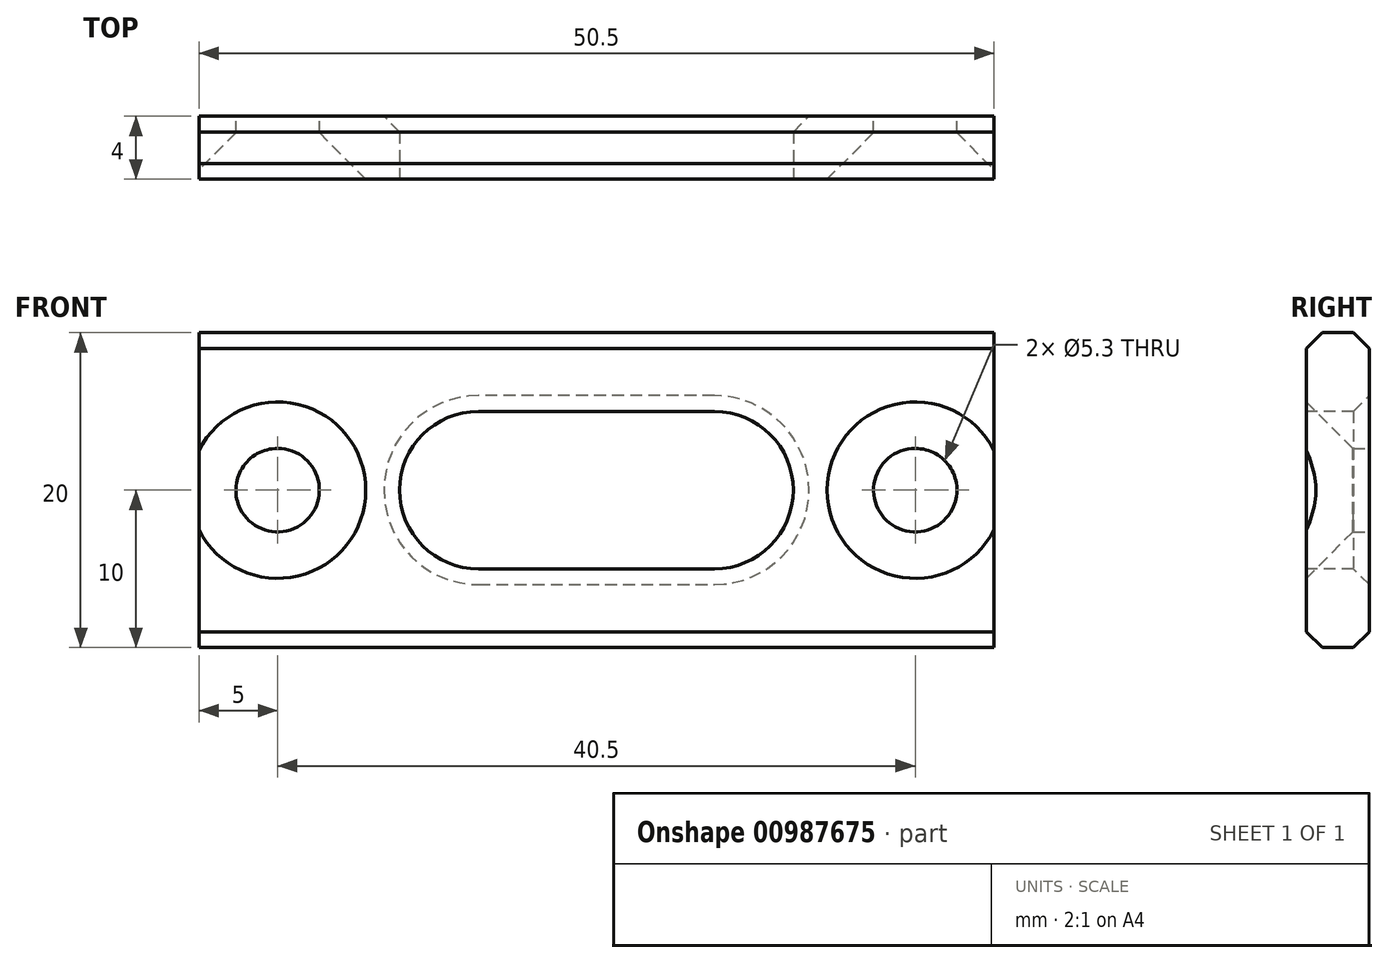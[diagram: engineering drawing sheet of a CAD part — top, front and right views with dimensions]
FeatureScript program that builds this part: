
annotation { "Feature Type Name" : "Feature", "Feature Type Description" : "" }
export const myFeature = defineFeature(function(context is Context, id is Id, definition is map)
    precondition{}
    {
        {
            var Q0;
            Q0=qCreatedBy(makeId("Front.planeOp"),FACE);
            var sketch = newSketch(context, id + "F0", { "sketchPlane" : qUnion([Q0])});
            skLineSegment(sketch, "E0.bottom", {"start": v(-25.25, 0) * mm, "end": v(25.25, 0) * mm});
            skLineSegment(sketch, "E0.top", {"start": v(-25.25, -20) * mm, "end": v(25.25, -20) * mm});
            skLineSegment(sketch, "E0.left", {"start": v(-25.25, 0) * mm, "end": v(-25.25, -20) * mm});
            skLineSegment(sketch, "E0.right", {"start": v(25.25, 0) * mm, "end": v(25.25, -20) * mm});
            skSolve(sketch);
        }
        {
            var Q0;
            Q0=makeQuery(id+"F0.imprint","IMPRINT",FACE,{"disambiguationData":[TD([[makeQuery(id+"F0.imprint","IMPRINT",EDGE,{"derivedFrom":sQuery(id+"F0.wireOp",EDGE,"E0.bottom")}),-1.0]])]});
            extrude(context, id + "F1", {"entities" : qUnion([Q0]), "depth" : 4 * mm, "offsetDistance" : 25 * mm});
        }
        {
            var Q0;
            Q0=makeQuery(id+"F1.opExtrude","CAP_FACE",FACE,{"disambiguationData":[OSD([sQuery(id+"F0.wireOp",EDGE,"E0.bottom"),sQuery(id+"F0.wireOp",EDGE,"E0.top"),sQuery(id+"F0.wireOp",EDGE,"E0.left"),sQuery(id+"F0.wireOp",EDGE,"E0.right")])],"isStart":false});
            var sketch = newSketch(context, id + "F2", { "sketchPlane" : qUnion([Q0])});
            skPoint(sketch, "E1", {"position": v(-20.25, -10) * mm});
            skPoint(sketch, "E2", {"position": v(20.25, -10) * mm});
            skSolve(sketch);
        }
        {
            var Q0;
            Q0=sQuery(id+"F2.wireOp",VERTEX,"E1");
            var Q1;
            Q1=sQuery(id+"F2.wireOp",VERTEX,"E2");
            var Q2;
            Q2=makeQuery(id+"F1.opExtrude","SWEPT_BODY",BODY,{"disambiguationData":[OSD([sQuery(id+"F0.wireOp",EDGE,"E0.bottom"),sQuery(id+"F0.wireOp",EDGE,"E0.top"),sQuery(id+"F0.wireOp",EDGE,"E0.left"),sQuery(id+"F0.wireOp",EDGE,"E0.right")])]});
            hole(context, id + "F3", {"style" : HoleStyle.C_SINK, "endStyle" : HoleEndStyle.BLIND, "standardTappedOrClearance" : lookupTablePath({ "fit" : "Close", "standard" : "ISO", "size" : "M5", "type" : "Clearance" }), "standardBlindInLast" : lookupTablePath({ "fit" : "Close", "standard" : "ISO", "engagement" : "75%", "pitch" : "0.8 mm", "size" : "M5", "type" : "Clearance & tapped" }), "holeDiameter" : 5.3 * mm, "cSinkDiameter" : 11.2 * mm, "cSinkAngle" : 90 * degree, "majorDiameter" : 8 * mm, "holeDepth" : 8 * mm, "isTappedThrough" : true, "tappedDepth" : 5 * mm, "tapClearance" : 3, "locations" : qUnion([Q0, Q1]), "scope" : qUnion([Q2]), "startStyle" : HoleStartStyle.PART});
        }
        {
            var Q0;
            Q0=makeQuery(id+"F1.opExtrude","CAP_FACE",FACE,{"disambiguationData":[OSD([sQuery(id+"F0.wireOp",EDGE,"E0.bottom"),sQuery(id+"F0.wireOp",EDGE,"E0.top"),sQuery(id+"F0.wireOp",EDGE,"E0.left"),sQuery(id+"F0.wireOp",EDGE,"E0.right")])],"isStart":false});
            var sketch = newSketch(context, id + "F4", { "sketchPlane" : qUnion([Q0])});
            skArc(sketch, "E3", {"start": v(-7.5, -5) * mm, "mid": v(-12.5, -10) * mm, "end": v(-7.5, -15) * mm});
            skArc(sketch, "E4", {"start": v(7.5, -15) * mm, "mid": v(12.5, -10) * mm, "end": v(7.5, -5) * mm});
            skLineSegment(sketch, "E5", {"start": v(-7.5, -5) * mm, "end": v(7.5, -5) * mm});
            skLineSegment(sketch, "E6", {"start": v(-7.5, -15) * mm, "end": v(7.5, -15) * mm});
            skSolve(sketch);
        }
        {
            var Q0;
            Q0=makeQuery(id+"F4.imprint","IMPRINT",FACE,{"disambiguationData":[TD([[makeQuery(id+"F4.imprint","IMPRINT",EDGE,{"derivedFrom":sQuery(id+"F4.wireOp",EDGE,"E3")}),1.0]])]});
            extrude(context, id + "F5", {"entities" : qUnion([Q0]), "operationType" : NewBodyOperationType.REMOVE, "endBound" : BoundingType.THROUGH_ALL, "oppositeDirection" : true, "depth" : 25 * mm, "offsetDistance" : 25 * mm});
        }
        {
            var Q0;
            Q0=makeQuery(id+"F1.opExtrude","CAP_EDGE",EDGE,{"disambiguationData":[OSD([sQuery(id+"F0.wireOp",EDGE,"E0.top")])],"isStart":false});
            var Q1;
            Q1=makeQuery(id+"F1.opExtrude","CAP_EDGE",EDGE,{"disambiguationData":[OSD([sQuery(id+"F0.wireOp",EDGE,"E0.bottom")])],"isStart":false});
            var Q2;
            Q2=makeQuery(id+"F5.boolean.opBoolean","COPY",EDGE,{"derivedFrom":makeQuery(id+"F5.opExtrude","CAP_EDGE",EDGE,{"disambiguationData":[OSD([sQuery(id+"F4.wireOp",EDGE,"E6")])],"isStart":true})});
            var Q3;
            Q3=makeQuery(id+"F5.boolean.opBoolean","INTERSECT",EDGE,{"derivedFrom":[makeQuery(id+"F1.opExtrude","CAP_FACE",FACE,{"disambiguationData":[OSD([sQuery(id+"F0.wireOp",EDGE,"E0.bottom"),sQuery(id+"F0.wireOp",EDGE,"E0.top"),sQuery(id+"F0.wireOp",EDGE,"E0.left"),sQuery(id+"F0.wireOp",EDGE,"E0.right")])],"isStart":true}),makeQuery(id+"F5.opExtrude","SWEPT_FACE",FACE,{"disambiguationData":[OSD([sQuery(id+"F4.wireOp",EDGE,"E6")])]})]});
            var Q4;
            Q4=makeQuery(id+"F1.opExtrude","CAP_EDGE",EDGE,{"disambiguationData":[OSD([sQuery(id+"F0.wireOp",EDGE,"E0.top")])],"isStart":true});
            var Q5;
            Q5=makeQuery(id+"F1.opExtrude","CAP_EDGE",EDGE,{"disambiguationData":[OSD([sQuery(id+"F0.wireOp",EDGE,"E0.bottom")])],"isStart":true});
            chamfer(context, id + "F6", {"entities" : qUnion([Q0, Q1, Q2, Q3, Q4, Q5]), "width" : 1 * mm, "tangentPropagation" : true});
        }
    });
